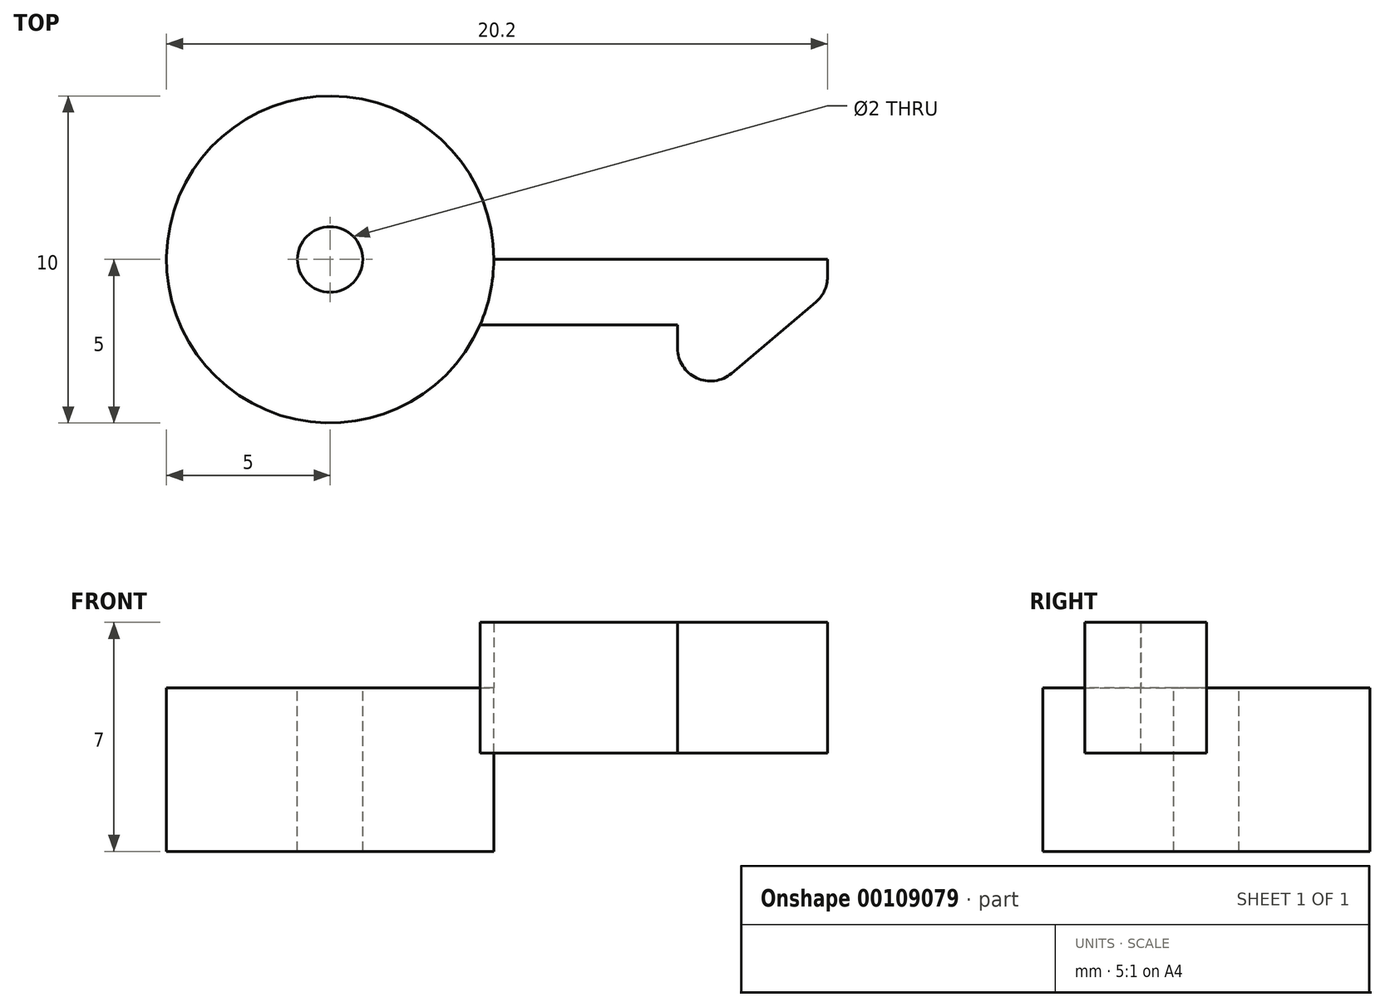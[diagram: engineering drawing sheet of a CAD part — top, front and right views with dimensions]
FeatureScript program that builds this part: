
annotation { "Feature Type Name" : "Feature", "Feature Type Description" : "" }
export const myFeature = defineFeature(function(context is Context, id is Id, definition is map)
    precondition{}
    {
        {
            var Q0;
            Q0=qCreatedBy(makeId("Top.planeOp"),FACE);
            var sketch = newSketch(context, id + "F0", { "sketchPlane" : qUnion([Q0])});
            skCircle(sketch, "E0", {"center": v(0, 0) * mm, "radius": 5 * mm});
            skLineSegment(sketch, "E1", {"start": v(5, 0) * mm, "end": v(13, 0) * mm});
            skLineSegment(sketch, "E2", {"start": v(13, 0) * mm, "end": v(15.2, 0) * mm});
            skLineSegment(sketch, "E3.MirrorCS", {"start": v(10.62, -4.88) * mm, "end": v(15.2, -1) * mm});
            skLineSegment(sketch, "E4.MirrorCS", {"start": v(15.2, 0) * mm, "end": v(15.2, -1) * mm});
            skLineSegment(sketch, "E5", {"start": v(10.62, -2) * mm, "end": v(10.62, -4.88) * mm});
            skPoint(sketch, "E6", {"position": v(4.58, -2) * mm});
            skLineSegment(sketch, "E7", {"start": v(4.58, -2) * mm, "end": v(10.62, -2) * mm});
            skSolve(sketch);
        }
        {
            var Q0;
            {var subQ0=sQuery(id+"F0.wireOp",EDGE,"E0");var subQ1=makeQuery(id+"F0.imprint","INTERSECT",VERTEX,{"derivedFrom":[subQ0,sQuery(id+"F0.wireOp",EDGE,"E1")]});Q0=makeQuery(id+"F0.imprint","IMPRINT",FACE,{"disambiguationData":[TD([[makeQuery(id+"F0.imprint","IMPRINT",EDGE,{"disambiguationData":[TD([[subQ1,-1.0]])],"derivedFrom":subQ0}),1.0]])]});}
            extrude(context, id + "F1", {"entities" : qUnion([Q0]), "oppositeDirection" : true, "depth" : 5 * mm});
        }
        {
            var Q0;
            {var subQ0=sQuery(id+"F0.wireOp",EDGE,"E1");Q0=makeQuery(id+"F0.imprint","IMPRINT",FACE,{"disambiguationData":[TD([[makeQuery(id+"F0.imprint","IMPRINT",EDGE,{"derivedFrom":subQ0}),-1.0]])]});}
            extrude(context, id + "F2", {"entities" : qUnion([Q0]), "operationType" : NewBodyOperationType.ADD, "oppositeDirection" : true, "depth" : 2 * mm});
        }
        {
            var Q0;
            Q0=makeQuery(id+"F0.imprint","IMPRINT",FACE,{"disambiguationData":[TD([[makeQuery(id+"F0.imprint","IMPRINT",EDGE,{"derivedFrom":sQuery(id+"F0.wireOp",EDGE,"E2")}),-1.0]])]});
            extrude(context, id + "F3", {"entities" : qUnion([Q0]), "operationType" : NewBodyOperationType.ADD, "endBound" : BoundingType.SYMMETRIC, "depth" : 4 * mm});
        }
        {
            var Q0;
            Q0=makeQuery(id+"F3.opExtrude","SWEPT_EDGE",EDGE,{"disambiguationData":[OSD([sQuery(id+"F0.wireOp",EDGE,"E3.MirrorCS"),sQuery(id+"F0.wireOp",EDGE,"092c0084-87fe-4148-8840-3697e8d49ca80.MirrorCS")])]});
            fillet(context, id + "F4", {"entities" : qUnion([Q0]), "radius" : 1 * mm, "tangentPropagation" : true, "allowEdgeOverflow" : false});
        }
        {
            var Q0;
            Q0=sQuery(id+"F0.wireOp",VERTEX,"E0.center");
            var Q1;
            Q1=makeQuery(id+"F1.opExtrude","SWEPT_BODY",BODY,{"disambiguationData":[OSD([sQuery(id+"F0.wireOp",EDGE,"E0")])]});
            hole(context, id + "F5", {"style" : HoleStyle.SIMPLE, "endStyle" : HoleEndStyle.THROUGH, "holeDiameter" : 2 * mm, "locations" : qUnion([Q0]), "scope" : qUnion([Q1]), "isTappedThrough" : true});
        }
    });
